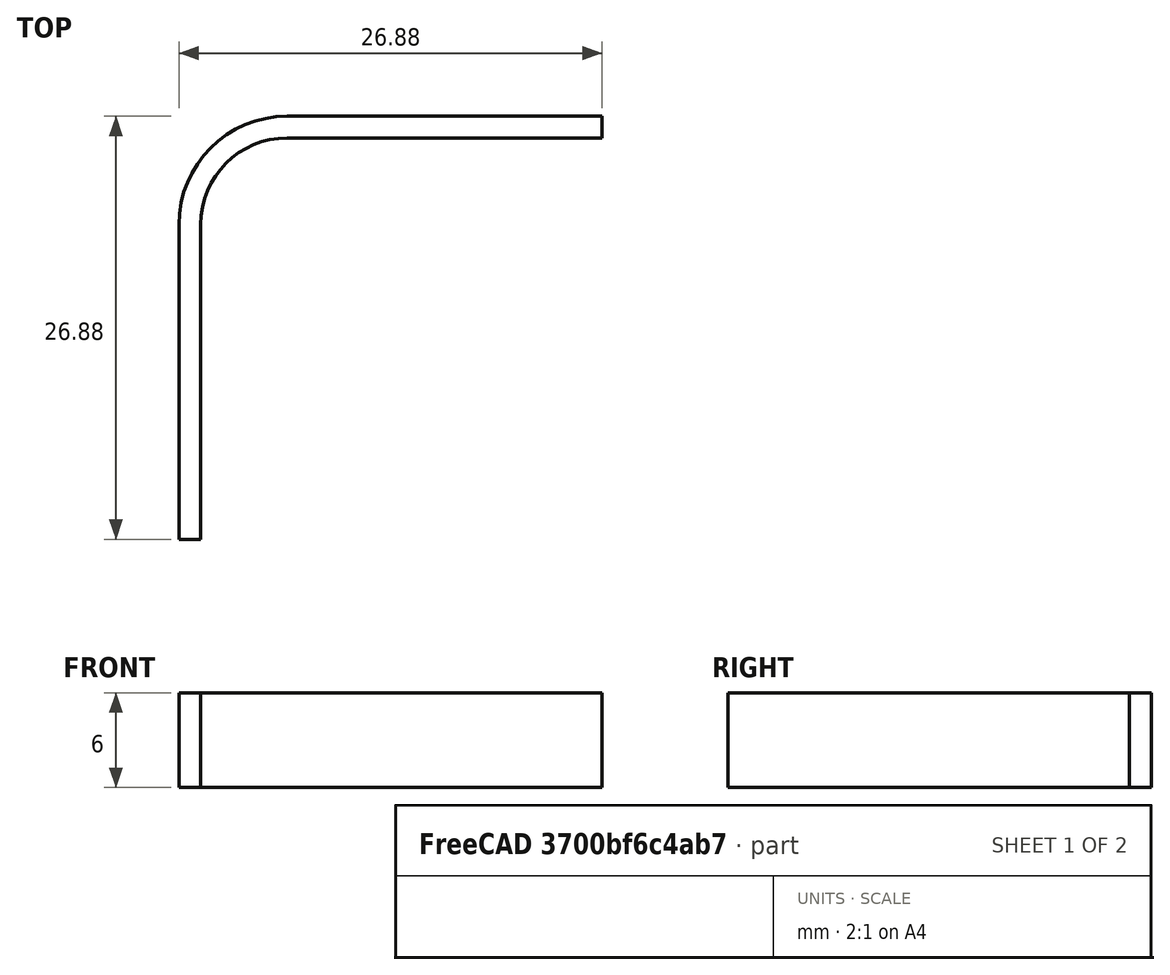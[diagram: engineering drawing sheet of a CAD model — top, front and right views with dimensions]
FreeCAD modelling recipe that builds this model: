
FCSTD DOCUMENT  (FreeCAD 0.20R27078 (Git))
Label: belt 20 toothed idler 90 deg
License: All rights reserved
LicenseURL: http://en.wikipedia.org/wiki/All_rights_reserved
objects: Sketcher::SketchObject×2, PartDesign::AdditivePipe×1, PartDesign::Body×1
note: 5 computed .brp shape members not serialized (recipe doc carries the construction recipe); baked Part::Feature solids carry a one-line shape summary decoded from their .brp

FEATURE [Sketcher::SketchObject] Sketch016
  FullyConstrained = true
  MapMode = 5
  Placement = pos=(0,0,0) rot=(1,0,0;1.5708rad)
  Support = -> [XZ_Plane010]
  sketch-geometry (4):
    g0: LineSegment StartX=0 StartY=6 StartZ=0 EndX=1.38 EndY=6 EndZ=0
    g1: LineSegment StartX=1.38 StartY=6 StartZ=0 EndX=1.38 EndY=0 EndZ=0
    g2: LineSegment StartX=1.38 StartY=0 StartZ=0 EndX=0 EndY=0 EndZ=0
    g3: LineSegment StartX=0 StartY=0 StartZ=0 EndX=0 EndY=6 EndZ=0
  constraints (12):
    c: Coincident(g0,g1)
    c: Coincident(g1,g2)
    c: Coincident(g2,g3)
    c: Coincident(g3,g0)
    c: Horizontal(g0)
    c: Horizontal(g2)
    c: Vertical(g1)
    c: Vertical(g3)
    c: PointOnObject(g0,g-2)
    c: PointOnObject(g1,g-1)
    c: DistanceY(g3,g3) = 6
    c: DistanceX(g0,g0) = 1.38
FEATURE [Sketcher::SketchObject] Sketch015
  ExternalGeometry = -> [Sketch016]
  FullyConstrained = true
  MapMode = 5
  Support = -> [XY_Plane010]
  sketch-geometry (3):
    g0: ArcOfCircle CenterX=6.88 CenterY=-1.3e-15 CenterZ=0 NormalX=0 NormalY=0 NormalZ=1 AngleXU=0 Radius=5.5 StartAngle=1.5708 EndAngle=3.14159
    g1: LineSegment StartX=1.38 StartY=-1.3e-15 StartZ=0 EndX=1.38 EndY=-20 EndZ=0
    g2: LineSegment StartX=6.88 StartY=5.5 StartZ=0 EndX=26.88 EndY=5.5 EndZ=0
  constraints (10):
    c: Coincident(g0,g-3)
    c: Horizontal(g0,g0)
    c: Vertical(g0,g0)
    c: Radius(g0) = 5.5
    c: Coincident(g1,g0)
    c: Vertical(g1)
    c: DistanceY(g1,g1) = 20
    c: Coincident(g2,g0)
    c: Horizontal(g2)
    c: Equal(g1,g2)
FEATURE [PartDesign::AdditivePipe] AdditivePipe005
  AuxilleryCurvelinear = true
  AuxillerySpineTangent = false
  Binormal = (0,0,0)
  Mode = 0
  Placement = pos=(0,0,0) rot=(1,0,0;1.5708rad)
  Profile = -> Sketch016
  Spine = -> Sketch015
  SpineTangent = false
  Transformation = 0
  Transition = 0
FEATURE [PartDesign::Body] Body010  label="belt 20 toothed idler 90 deg"
  Group = -> [Sketch016,Sketch015,AdditivePipe005]
  Origin = -> Origin010
  Tip = -> AdditivePipe005
